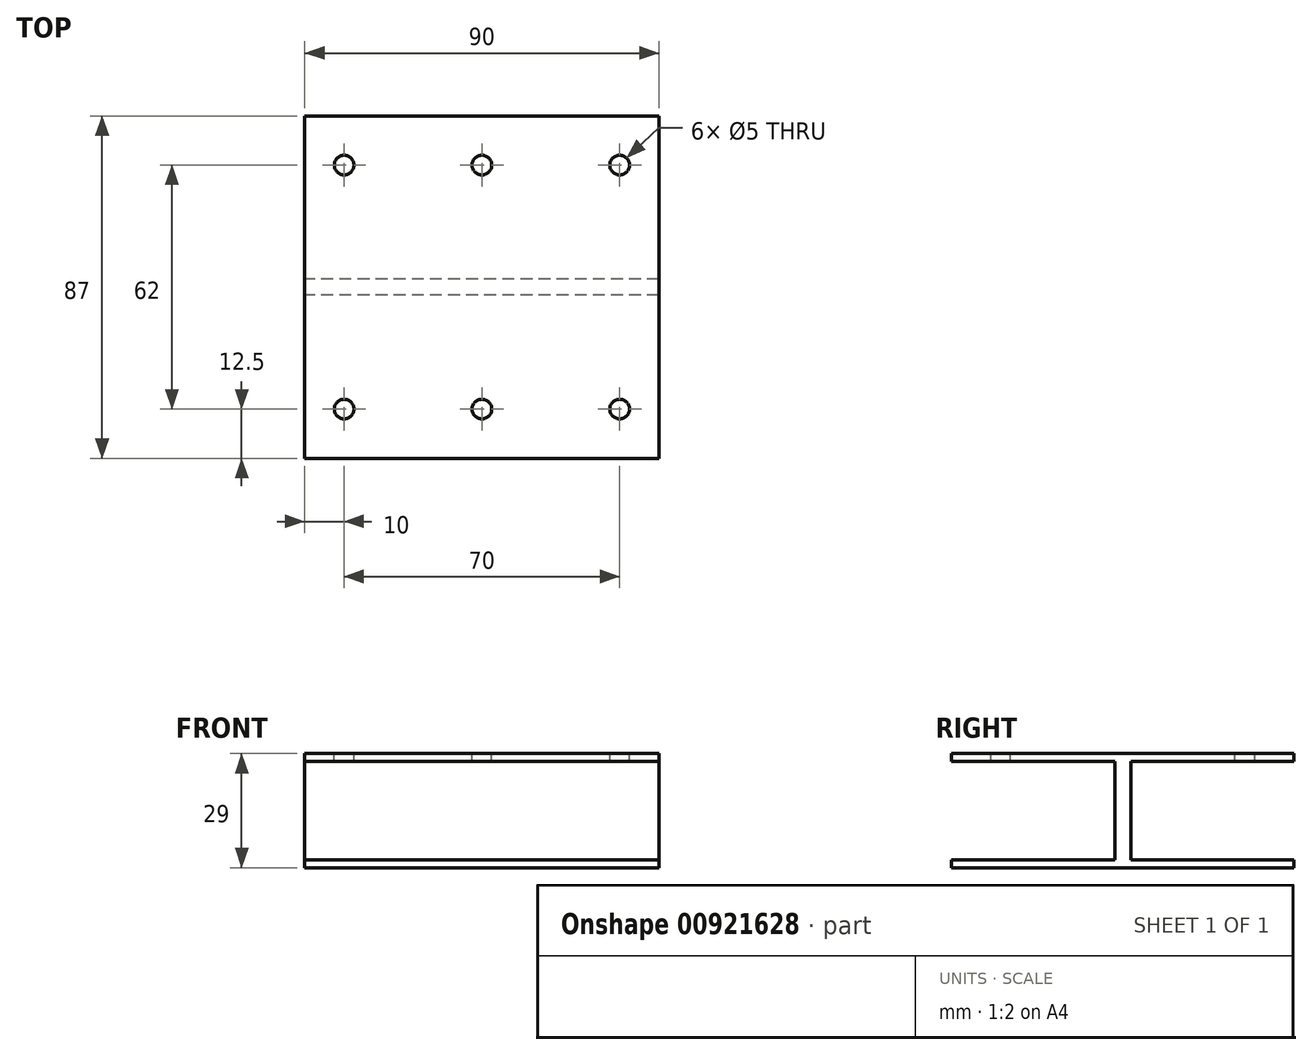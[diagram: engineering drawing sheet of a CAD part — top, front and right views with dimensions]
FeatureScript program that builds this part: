
annotation { "Feature Type Name" : "Feature", "Feature Type Description" : "" }
export const myFeature = defineFeature(function(context is Context, id is Id, definition is map)
    precondition{}
    {
        {
            var Q0;
            Q0=qCreatedBy(makeId("Right.planeOp"),FACE);
            var sketch = newSketch(context, id + "F0", { "sketchPlane" : qUnion([Q0])});
            skLineSegment(sketch, "E0", {"start": v(0, 0) * mm, "end": v(-43.5, 0) * mm});
            skLineSegment(sketch, "E1", {"start": v(0, 0) * mm, "end": v(0, -29) * mm});
            skLineSegment(sketch, "E2", {"start": v(0, -29) * mm, "end": v(-43.5, -29) * mm});
            skLineSegment(sketch, "E3", {"start": v(-43.5, 0) * mm, "end": v(-43.5, -2) * mm});
            skLineSegment(sketch, "E4", {"start": v(-43.5, -2) * mm, "end": v(-2, -2) * mm});
            skLineSegment(sketch, "E5", {"start": v(-2, -2) * mm, "end": v(-2, -27) * mm});
            skLineSegment(sketch, "E6", {"start": v(-2, -27) * mm, "end": v(-43.5, -27) * mm});
            skLineSegment(sketch, "E7", {"start": v(-43.5, -27) * mm, "end": v(-43.5, -29) * mm});
            skLineSegment(sketch, "E8", {"start": v(-2, -2) * mm, "end": v(0, -2) * mm, "construction": true});
            skSolve(sketch);
        }
        {
            var Q0;
            Q0 = qSketchRegion(id + "F0", true);
            extrude(context, id + "F1", {"entities" : qUnion([Q0]), "endBound" : BoundingType.SYMMETRIC, "depth" : 90 * mm, "offsetDistance" : 25 * mm});
        }
        {
            var Q0;
            Q0=makeQuery(id+"F1.opExtrude","SWEPT_BODY",BODY,{"disambiguationData":[OSD([sQuery(id+"F0.wireOp",EDGE,"E0"),sQuery(id+"F0.wireOp",EDGE,"E1"),sQuery(id+"F0.wireOp",EDGE,"E2"),sQuery(id+"F0.wireOp",EDGE,"E3"),sQuery(id+"F0.wireOp",EDGE,"E4"),sQuery(id+"F0.wireOp",EDGE,"E5"),sQuery(id+"F0.wireOp",EDGE,"E6"),sQuery(id+"F0.wireOp",EDGE,"E7")])]});
            var Q1;
            Q1=qCreatedBy(makeId("Front.planeOp"),FACE);
            mirror(context, id + "F2", {"operationType" : NewBodyOperationType.ADD, "entities" : qUnion([Q0]), "mirrorPlane" : qUnion([Q1])});
        }
        {
            var Q0;
            {var subQ0=makeQuery(id+"F1.opExtrude","SWEPT_FACE",FACE,{"disambiguationData":[OSD([sQuery(id+"F0.wireOp",EDGE,"E0")])]});Q0=makeQuery(id+"F2.boolean.opBoolean","MERGE",FACE,{"derivedFrom":[subQ0,makeQuery(id+"F2.opPattern","COPY",FACE,{"derivedFrom":subQ0,"instanceName":"1"})]});}
            var sketch = newSketch(context, id + "F3", { "sketchPlane" : qUnion([Q0])});
            skCircle(sketch, "E9", {"center": v(35, 31) * mm, "radius": 2.5 * mm});
            skCircle(sketch, "E10", {"center": v(0, 31) * mm, "radius": 2.5 * mm});
            skCircle(sketch, "E11", {"center": v(-35, 31) * mm, "radius": 2.5 * mm});
            skCircle(sketch, "E12", {"center": v(-35, -31) * mm, "radius": 2.5 * mm});
            skCircle(sketch, "E13", {"center": v(0, -31) * mm, "radius": 2.5 * mm});
            skCircle(sketch, "E14", {"center": v(35, -31) * mm, "radius": 2.5 * mm});
            skLineSegment(sketch, "E15", {"start": v(0, 0) * mm, "end": v(-52.03, 0) * mm, "construction": true});
            skSolve(sketch);
        }
        {
            var Q0;
            Q0 = qSketchRegion(id + "F3", true);
            extrude(context, id + "F4", {"entities" : qUnion([Q0]), "operationType" : NewBodyOperationType.REMOVE, "endBound" : BoundingType.UP_TO_NEXT, "oppositeDirection" : true, "depth" : 25 * mm, "offsetDistance" : 25 * mm});
        }
    });
